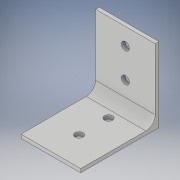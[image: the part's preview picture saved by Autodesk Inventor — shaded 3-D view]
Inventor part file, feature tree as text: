
AUTODESK INVENTOR PART (.ipt)
format: ipt  version: 2019 (Build 230136000, 136)  size: 136,704 bytes
history: native  units: in
note: dims shown in document units (in); Inventor stores cm internally (conversion verified against a paired STEP export)
features: extrude x4, sketch x4, fillet x1
ambient origin geometry x8: Origin, YZ Plane, XZ Plane, XY Plane, X Axis, Y Axis, Z Axis, Center Point
bodies: Solid1 (feature_tree)
feature tree (9):
  extrude  "Extrusion1"  Depth=0.8in
  extrude  "Extrusion2"  Depth=0.05in
  extrude  "Extrusion3"  Depth=1.0in
  fillet  "Fillet1"  Radius=0.107in
  sketch  "Sketch1"  dims[d0=1.0in d1=0.8in]
  sketch  "Sketch2"  dims[d2=0.05in d3=0.0in d4=0.05in]
  sketch  "Sketch3"  dims[d5=1.0in d6=0.0in d7=0.107in d8=0.107in]
  sketch  "Sketch4"  dims[d9=0.4in d10=0.4in d11=0.394in d12=0.379in d13=1.0in d14=0.0in d15=0.107in d16=0.379in d17=0.394in d18=0.4in d19=0.107in d20=0.4in d22=0.0in d23=1.0in d24=0.125in]
  extrude  "Extrusion4"  Depth=0.125in
